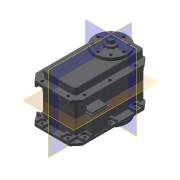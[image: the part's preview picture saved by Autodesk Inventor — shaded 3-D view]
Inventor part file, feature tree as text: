
AUTODESK INVENTOR PART (.ipt)
format: ipt  version: 2020 (Build 240168000, 168)  size: 719,872 bytes
history: native  units: mm (DEFAULTED — no unit token found)
features: other x6, sketch x3, extrude x2
ambient origin geometry x8: Origin, YZ Plane, XZ Plane, XY Plane, X Axis, Y Axis, Z Axis, Center Point
bodies: Body1 (feature_tree)
feature tree (11):
  other  "솔리드1"
  other  "기준1"
  other  "작업 평면1"
  other  "작업 평면2"
  sketch  "스케치1"
  other  "작업 평면3"
  extrude  "돌출1"  [1 undecoded]
  extrude  "돌출2"  [1 undecoded]
  other  "작업 평면4"
  sketch  "스케치2"
  sketch  "스케치3"
note: 2 required parameter values undecoded (feature->parameter linkage not recoverable at this tier; creation-order binding heuristic only, values carry confidence <= 0.55)
